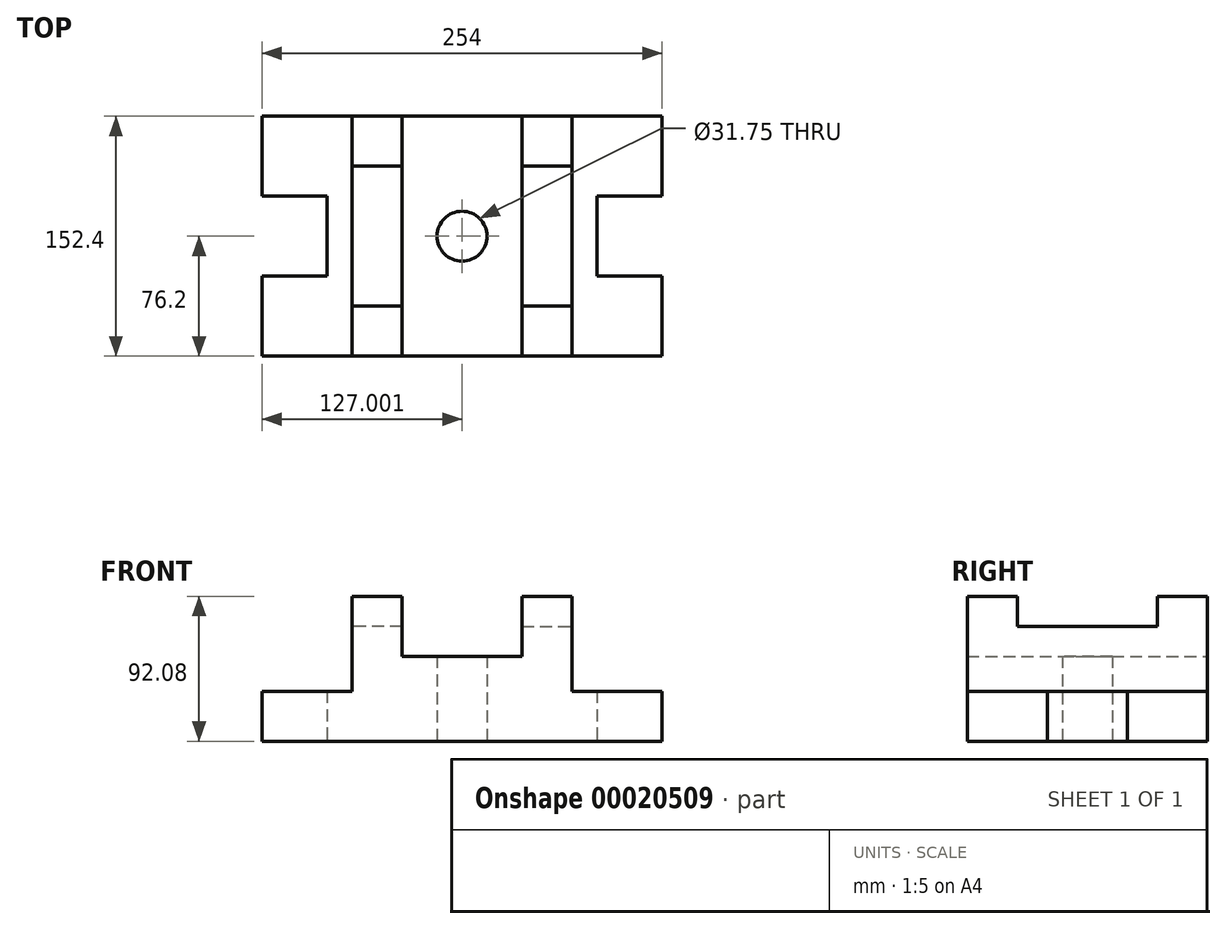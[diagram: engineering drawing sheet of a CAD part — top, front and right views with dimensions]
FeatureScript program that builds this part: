
annotation { "Feature Type Name" : "Feature", "Feature Type Description" : "" }
export const myFeature = defineFeature(function(context is Context, id is Id, definition is map)
    precondition{}
    {
        {
            var Q0;
            Q0=qCreatedBy(makeId("Top.planeOp"),FACE);
            var sketch = newSketch(context, id + "F0", { "sketchPlane" : qUnion([Q0])});
            skLineSegment(sketch, "E0", {"start": v(-57.69, -31.75) * mm, "end": v(69.31, -31.75) * mm});
            skLineSegment(sketch, "E1", {"start": v(69.31, -31.75) * mm, "end": v(69.31, 19.05) * mm});
            skLineSegment(sketch, "E2", {"start": v(69.31, 19.05) * mm, "end": v(28.04, 19.05) * mm});
            skLineSegment(sketch, "E3", {"start": v(28.04, 19.05) * mm, "end": v(28.04, 44.45) * mm});
            skLineSegment(sketch, "E4", {"start": v(28.04, 44.45) * mm, "end": v(-41.81, 44.45) * mm});
            skLineSegment(sketch, "E5", {"start": v(-57.69, 28.57) * mm, "end": v(-57.69, -31.75) * mm});
            skArc(sketch, "E6", {"start": v(-57.69, 28.57) * mm, "mid": v(-46.46, 33.22) * mm, "end": v(-41.81, 44.45) * mm});
            skPoint(sketch, "E7", {"position": v(12.16, -31.75) * mm});
            skPoint(sketch, "E8", {"position": v(-19.59, -31.75) * mm});
            skLineSegment(sketch, "E9", {"start": v(-19.59, -31.75) * mm, "end": v(-19.59, 44.45) * mm});
            skLineSegment(sketch, "E10", {"start": v(12.16, -31.75) * mm, "end": v(12.16, 44.45) * mm});
            skPoint(sketch, "E11", {"position": v(-19.59, 0) * mm});
            skLineSegment(sketch, "E12", {"start": v(-19.59, 0) * mm, "end": v(12.16, 0) * mm});
            skSolve(sketch);
        }
        {
            var Q0;
            {var subQ7=sQuery(id+"F0.wireOp",EDGE,"E1");Q0=makeQuery(id+"F0.imprint","IMPRINT",FACE,{"disambiguationData":[TD([[makeQuery(id+"F0.imprint","IMPRINT",EDGE,{"derivedFrom":subQ7}),1.0]])]});}
            extrude(context, id + "F1", {"entities" : qUnion([Q0]), "depth" : 31.75 * mm});
        }
        {
            var Q0;
            {var subQ0=sQuery(id+"F0.wireOp",EDGE,"E12");Q0=makeQuery(id+"F0.imprint","IMPRINT",FACE,{"disambiguationData":[TD([[makeQuery(id+"F0.imprint","IMPRINT",EDGE,{"derivedFrom":subQ0}),-1.0]])]});}
            extrude(context, id + "F2", {"entities" : qUnion([Q0]), "operationType" : NewBodyOperationType.ADD, "depth" : 92.07 * mm});
        }
        {
            var Q0;
            {var subQ0=sQuery(id+"F0.wireOp",EDGE,"E12");Q0=makeQuery(id+"F0.imprint","IMPRINT",FACE,{"disambiguationData":[TD([[makeQuery(id+"F0.imprint","IMPRINT",EDGE,{"derivedFrom":subQ0}),1.0]])]});}
            extrude(context, id + "F3", {"entities" : qUnion([Q0]), "operationType" : NewBodyOperationType.ADD, "depth" : 73.02 * mm});
        }
        {
            var Q0;
            {var subQ7=sQuery(id+"F0.wireOp",EDGE,"E5");Q0=makeQuery(id+"F0.imprint","IMPRINT",FACE,{"disambiguationData":[TD([[makeQuery(id+"F0.imprint","IMPRINT",EDGE,{"derivedFrom":subQ7}),1.0]])]});}
            extrude(context, id + "F4", {"entities" : qUnion([Q0]), "operationType" : NewBodyOperationType.ADD, "depth" : 53.97 * mm});
        }
        {
            var Q0;
            Q0=makeQuery(id+"F1.opExtrude","SWEPT_BODY",BODY,{"disambiguationData":[OSD([sQuery(id+"F0.wireOp",EDGE,"E0"),sQuery(id+"F0.wireOp",EDGE,"E1"),sQuery(id+"F0.wireOp",EDGE,"E2"),sQuery(id+"F0.wireOp",EDGE,"E3"),sQuery(id+"F0.wireOp",EDGE,"E4"),sQuery(id+"F0.wireOp",EDGE,"E10")])]});
            var Q1;
            Q1=makeQuery(id+"F4.opExtrude","SWEPT_FACE",FACE,{"disambiguationData":[OSD([sQuery(id+"F0.wireOp",EDGE,"E5")])]});
            mirror(context, id + "F5", {"operationType" : NewBodyOperationType.ADD, "entities" : qUnion([Q0]), "mirrorPlane" : qUnion([Q1])});
        }
        {
            var Q0;
            Q0=makeQuery(id+"F1.opExtrude","SWEPT_BODY",BODY,{"disambiguationData":[OSD([sQuery(id+"F0.wireOp",EDGE,"E0"),sQuery(id+"F0.wireOp",EDGE,"E1"),sQuery(id+"F0.wireOp",EDGE,"E2"),sQuery(id+"F0.wireOp",EDGE,"E3"),sQuery(id+"F0.wireOp",EDGE,"E4"),sQuery(id+"F0.wireOp",EDGE,"E10")])]});
            var Q1;
            {var subQ0=sQuery(id+"F0.wireOp",EDGE,"E4");Q1=makeQuery(id+"F4.boolean.opBoolean","MERGE",FACE,{"derivedFrom":[makeQuery(id+"F3.boolean.opBoolean","MERGE",FACE,{"derivedFrom":[makeQuery(id+"F1.opExtrude","SWEPT_FACE",FACE,{"disambiguationData":[OSD([subQ0])]}),makeQuery(id+"F3.opExtrude","SWEPT_FACE",FACE,{"disambiguationData":[OSD([subQ0])]})]}),makeQuery(id+"F4.opExtrude","SWEPT_FACE",FACE,{"disambiguationData":[OSD([subQ0])]})]});}
            mirror(context, id + "F6", {"operationType" : NewBodyOperationType.ADD, "entities" : qUnion([Q0]), "mirrorPlane" : qUnion([Q1])});
        }
    });
